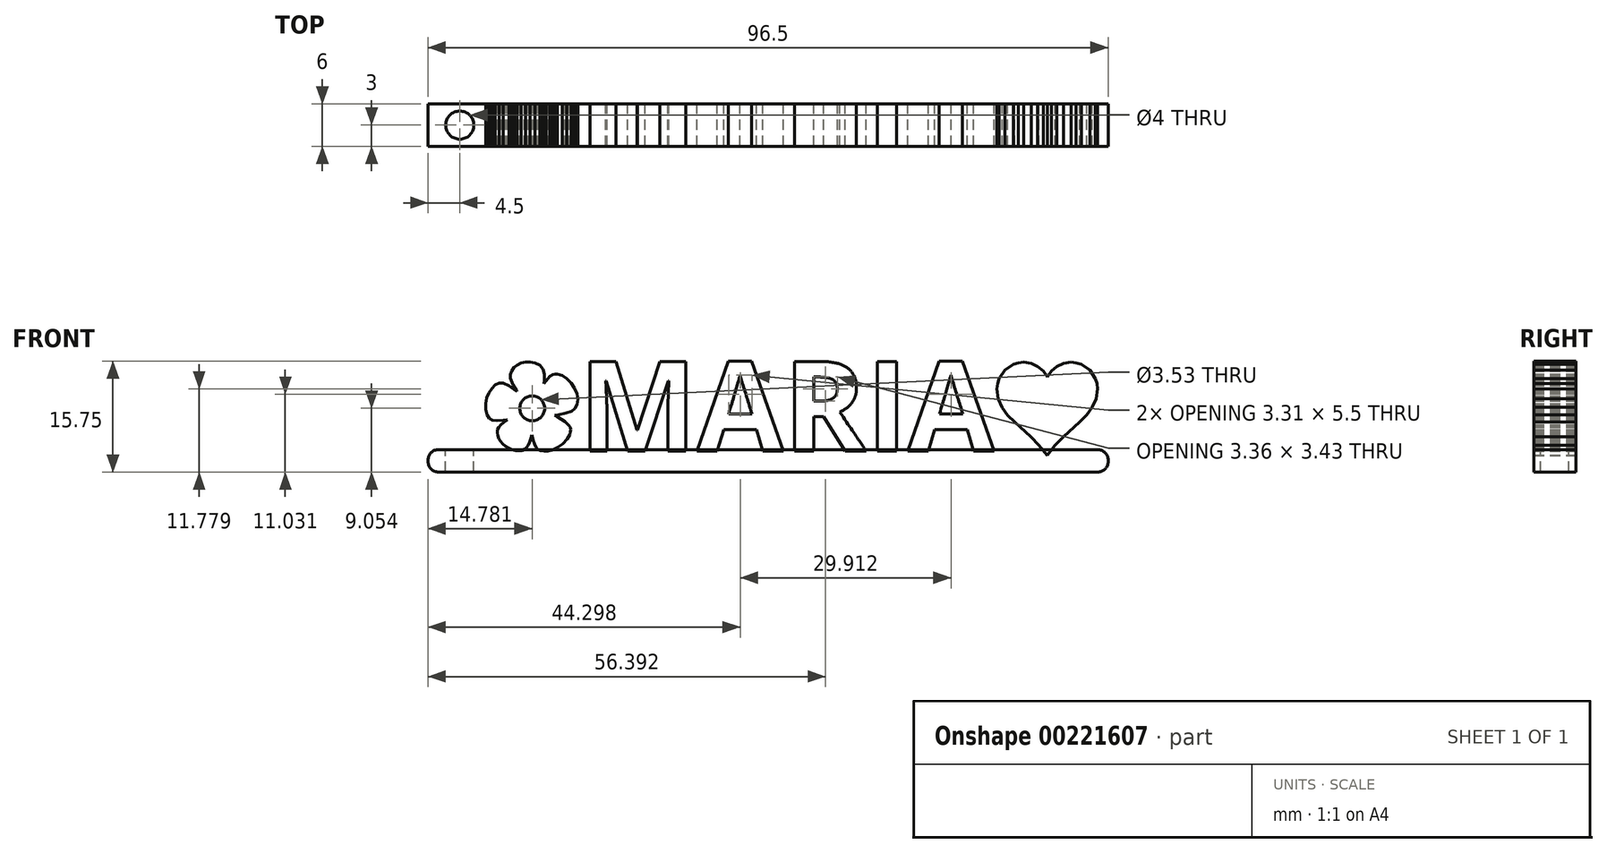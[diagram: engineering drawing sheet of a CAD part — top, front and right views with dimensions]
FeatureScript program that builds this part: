
annotation { "Feature Type Name" : "Feature", "Feature Type Description" : "" }
export const myFeature = defineFeature(function(context is Context, id is Id, definition is map)
    precondition{}
    {
        {
            var Q0;
            Q0=qCreatedBy(makeId("Front.planeOp"),FACE);
            var sketch = newSketch(context, id + "F0", { "sketchPlane" : qUnion([Q0])});
            skText(sketch, "E0", { "text": "   MARIA", "fontName": "OpenSans-Bold.ttf"});
            skLineSegment(sketch, "E1.0.0", {"start": v(-9.3, 0.1) * mm, "end": v(-8.53, 0.46) * mm});
            skLineSegment(sketch, "E1.0.1", {"start": v(-8.53, 0.46) * mm, "end": v(-7.79, 1.02) * mm});
            skLineSegment(sketch, "E1.0.2", {"start": v(-7.79, 1.02) * mm, "end": v(-7.18, 1.67) * mm});
            skLineSegment(sketch, "E1.0.3", {"start": v(-7.18, 1.67) * mm, "end": v(-6.78, 2.35) * mm});
            skLineSegment(sketch, "E1.0.4", {"start": v(-6.78, 2.35) * mm, "end": v(-6.68, 2.7) * mm});
            skLineSegment(sketch, "E1.0.5", {"start": v(-6.68, 2.7) * mm, "end": v(-6.67, 3.02) * mm});
            skLineSegment(sketch, "E1.0.6", {"start": v(-6.67, 3.02) * mm, "end": v(-6.73, 3.33) * mm});
            skLineSegment(sketch, "E1.0.7", {"start": v(-6.73, 3.33) * mm, "end": v(-6.89, 3.62) * mm});
            skLineSegment(sketch, "E1.0.8", {"start": v(-6.89, 3.62) * mm, "end": v(-7.48, 4.2) * mm});
            skLineSegment(sketch, "E1.0.9", {"start": v(-7.48, 4.2) * mm, "end": v(-8.5, 4.79) * mm});
            skLineSegment(sketch, "E1.0.10", {"start": v(-8.5, 4.79) * mm, "end": v(-8.93, 5.06) * mm});
            skLineSegment(sketch, "E1.0.11", {"start": v(-8.93, 5.06) * mm, "end": v(-8.42, 5.16) * mm});
            skLineSegment(sketch, "E1.0.12", {"start": v(-8.42, 5.16) * mm, "end": v(-7.31, 5.37) * mm});
            skLineSegment(sketch, "E1.0.13", {"start": v(-7.31, 5.37) * mm, "end": v(-6.55, 5.65) * mm});
            skLineSegment(sketch, "E1.0.14", {"start": v(-6.55, 5.65) * mm, "end": v(-6.05, 6.04) * mm});
            skLineSegment(sketch, "E1.0.15", {"start": v(-6.05, 6.04) * mm, "end": v(-5.76, 6.58) * mm});
            skLineSegment(sketch, "E1.0.16", {"start": v(-5.76, 6.58) * mm, "end": v(-5.64, 7.33) * mm});
            skLineSegment(sketch, "E1.0.17", {"start": v(-5.64, 7.33) * mm, "end": v(-5.78, 8.14) * mm});
            skLineSegment(sketch, "E1.0.18", {"start": v(-5.78, 8.14) * mm, "end": v(-6.1, 8.93) * mm});
            skLineSegment(sketch, "E1.0.19", {"start": v(-6.1, 8.93) * mm, "end": v(-6.6, 9.67) * mm});
            skLineSegment(sketch, "E1.0.20", {"start": v(-6.6, 9.67) * mm, "end": v(-7.2, 10.28) * mm});
            skLineSegment(sketch, "E1.0.21", {"start": v(-7.2, 10.28) * mm, "end": v(-7.86, 10.72) * mm});
            skLineSegment(sketch, "E1.0.22", {"start": v(-7.86, 10.72) * mm, "end": v(-8.55, 10.93) * mm});
            skLineSegment(sketch, "E1.0.23", {"start": v(-8.55, 10.93) * mm, "end": v(-8.88, 10.93) * mm});
            skLineSegment(sketch, "E1.0.24", {"start": v(-8.88, 10.93) * mm, "end": v(-9.2, 10.85) * mm});
            skLineSegment(sketch, "E1.0.25", {"start": v(-9.2, 10.85) * mm, "end": v(-9.65, 10.56) * mm});
            skLineSegment(sketch, "E1.0.26", {"start": v(-9.65, 10.56) * mm, "end": v(-10.14, 9.98) * mm});
            skLineSegment(sketch, "E1.0.27", {"start": v(-10.14, 9.98) * mm, "end": v(-10.45, 9.58) * mm});
            skLineSegment(sketch, "E1.0.28", {"start": v(-10.45, 9.58) * mm, "end": v(-10.4, 10.03) * mm});
            skLineSegment(sketch, "E1.0.29", {"start": v(-10.4, 10.03) * mm, "end": v(-10.4, 10.93) * mm});
            skLineSegment(sketch, "E1.0.30", {"start": v(-10.4, 10.93) * mm, "end": v(-10.6, 11.63) * mm});
            skLineSegment(sketch, "E1.0.31", {"start": v(-10.6, 11.63) * mm, "end": v(-11.04, 12.15) * mm});
            skLineSegment(sketch, "E1.0.32", {"start": v(-11.04, 12.15) * mm, "end": v(-11.71, 12.5) * mm});
            skLineSegment(sketch, "E1.0.33", {"start": v(-11.71, 12.5) * mm, "end": v(-12.4, 12.64) * mm});
            skLineSegment(sketch, "E1.0.34", {"start": v(-12.4, 12.64) * mm, "end": v(-13.07, 12.62) * mm});
            skLineSegment(sketch, "E1.0.35", {"start": v(-13.07, 12.62) * mm, "end": v(-13.7, 12.47) * mm});
            skLineSegment(sketch, "E1.0.36", {"start": v(-13.7, 12.47) * mm, "end": v(-14.26, 12.2) * mm});
            skLineSegment(sketch, "E1.0.37", {"start": v(-14.26, 12.2) * mm, "end": v(-14.72, 11.83) * mm});
            skLineSegment(sketch, "E1.0.38", {"start": v(-14.72, 11.83) * mm, "end": v(-15.05, 11.38) * mm});
            skLineSegment(sketch, "E1.0.39", {"start": v(-15.05, 11.38) * mm, "end": v(-15.22, 10.87) * mm});
            skLineSegment(sketch, "E1.0.40", {"start": v(-15.22, 10.87) * mm, "end": v(-15.2, 10.3) * mm});
            skLineSegment(sketch, "E1.0.41", {"start": v(-15.2, 10.3) * mm, "end": v(-14.83, 9.4) * mm});
            skLineSegment(sketch, "E1.0.42", {"start": v(-14.83, 9.4) * mm, "end": v(-14.35, 8.55) * mm});
            skLineSegment(sketch, "E1.0.43", {"start": v(-14.35, 8.55) * mm, "end": v(-14.3, 8.4) * mm});
            skLineSegment(sketch, "E1.0.44", {"start": v(-14.3, 8.4) * mm, "end": v(-14.48, 8.53) * mm});
            skLineSegment(sketch, "E1.0.45", {"start": v(-14.48, 8.53) * mm, "end": v(-15.4, 9.23) * mm});
            skLineSegment(sketch, "E1.0.46", {"start": v(-15.4, 9.23) * mm, "end": v(-16.22, 9.63) * mm});
            skLineSegment(sketch, "E1.0.47", {"start": v(-16.22, 9.63) * mm, "end": v(-16.8, 9.63) * mm});
            skLineSegment(sketch, "E1.0.48", {"start": v(-16.8, 9.63) * mm, "end": v(-17.36, 9.37) * mm});
            skLineSegment(sketch, "E1.0.49", {"start": v(-17.36, 9.37) * mm, "end": v(-17.85, 8.9) * mm});
            skLineSegment(sketch, "E1.0.50", {"start": v(-17.85, 8.9) * mm, "end": v(-18.26, 8.26) * mm});
            skLineSegment(sketch, "E1.0.51", {"start": v(-18.26, 8.26) * mm, "end": v(-18.56, 7.51) * mm});
            skLineSegment(sketch, "E1.0.52", {"start": v(-18.56, 7.51) * mm, "end": v(-18.72, 6.71) * mm});
            skLineSegment(sketch, "E1.0.53", {"start": v(-18.72, 6.71) * mm, "end": v(-18.72, 5.9) * mm});
            skLineSegment(sketch, "E1.0.54", {"start": v(-18.72, 5.9) * mm, "end": v(-18.52, 5.16) * mm});
            skLineSegment(sketch, "E1.0.55", {"start": v(-18.52, 5.16) * mm, "end": v(-18.2, 4.64) * mm});
            skLineSegment(sketch, "E1.0.56", {"start": v(-18.2, 4.64) * mm, "end": v(-17.75, 4.36) * mm});
            skLineSegment(sketch, "E1.0.57", {"start": v(-17.75, 4.36) * mm, "end": v(-17.1, 4.27) * mm});
            skLineSegment(sketch, "E1.0.58", {"start": v(-17.1, 4.27) * mm, "end": v(-16.21, 4.37) * mm});
            skLineSegment(sketch, "E1.0.59", {"start": v(-16.21, 4.37) * mm, "end": v(-15.7, 4.43) * mm});
            skLineSegment(sketch, "E1.0.60", {"start": v(-15.7, 4.43) * mm, "end": v(-15.67, 4.4) * mm});
            skLineSegment(sketch, "E1.0.61", {"start": v(-15.67, 4.4) * mm, "end": v(-15.78, 4.33) * mm});
            skLineSegment(sketch, "E1.0.62", {"start": v(-15.78, 4.33) * mm, "end": v(-16.17, 4.07) * mm});
            skLineSegment(sketch, "E1.0.63", {"start": v(-16.17, 4.07) * mm, "end": v(-16.55, 3.71) * mm});
            skLineSegment(sketch, "E1.0.64", {"start": v(-16.55, 3.71) * mm, "end": v(-16.87, 3.33) * mm});
            skLineSegment(sketch, "E1.0.65", {"start": v(-16.87, 3.33) * mm, "end": v(-17.04, 3) * mm});
            skLineSegment(sketch, "E1.0.66", {"start": v(-17.04, 3) * mm, "end": v(-17.08, 2.6) * mm});
            skLineSegment(sketch, "E1.0.67", {"start": v(-17.08, 2.6) * mm, "end": v(-17.02, 2.2) * mm});
            skLineSegment(sketch, "E1.0.68", {"start": v(-17.02, 2.2) * mm, "end": v(-16.87, 1.78) * mm});
            skLineSegment(sketch, "E1.0.69", {"start": v(-16.87, 1.78) * mm, "end": v(-16.62, 1.39) * mm});
            skLineSegment(sketch, "E1.0.70", {"start": v(-16.62, 1.39) * mm, "end": v(-16.3, 1.02) * mm});
            skLineSegment(sketch, "E1.0.71", {"start": v(-16.3, 1.02) * mm, "end": v(-15.9, 0.69) * mm});
            skLineSegment(sketch, "E1.0.72", {"start": v(-15.9, 0.69) * mm, "end": v(-15.45, 0.4) * mm});
            skLineSegment(sketch, "E1.0.73", {"start": v(-15.45, 0.4) * mm, "end": v(-14.95, 0.2) * mm});
            skLineSegment(sketch, "E1.0.74", {"start": v(-14.95, 0.2) * mm, "end": v(-14.44, 0.06) * mm});
            skLineSegment(sketch, "E1.0.75", {"start": v(-14.44, 0.06) * mm, "end": v(-13.98, 0.02) * mm});
            skLineSegment(sketch, "E1.0.76", {"start": v(-13.98, 0.02) * mm, "end": v(-13.58, 0.08) * mm});
            skLineSegment(sketch, "E1.0.77", {"start": v(-13.58, 0.08) * mm, "end": v(-13.23, 0.23) * mm});
            skLineSegment(sketch, "E1.0.78", {"start": v(-13.23, 0.23) * mm, "end": v(-12.92, 0.49) * mm});
            skLineSegment(sketch, "E1.0.79", {"start": v(-12.92, 0.49) * mm, "end": v(-12.67, 0.84) * mm});
            skLineSegment(sketch, "E1.0.80", {"start": v(-12.67, 0.84) * mm, "end": v(-12.46, 1.28) * mm});
            skLineSegment(sketch, "E1.0.81", {"start": v(-12.46, 1.28) * mm, "end": v(-12.3, 1.83) * mm});
            skLineSegment(sketch, "E1.0.82", {"start": v(-12.3, 1.83) * mm, "end": v(-12.19, 2.26) * mm});
            skLineSegment(sketch, "E1.0.83", {"start": v(-12.19, 2.26) * mm, "end": v(-12.13, 2.1) * mm});
            skLineSegment(sketch, "E1.0.84", {"start": v(-12.13, 2.1) * mm, "end": v(-12.01, 1.53) * mm});
            skLineSegment(sketch, "E1.0.85", {"start": v(-12.01, 1.53) * mm, "end": v(-11.82, 1) * mm});
            skLineSegment(sketch, "E1.0.86", {"start": v(-11.82, 1) * mm, "end": v(-11.6, 0.55) * mm});
            skLineSegment(sketch, "E1.0.87", {"start": v(-11.6, 0.55) * mm, "end": v(-11.35, 0.26) * mm});
            skLineSegment(sketch, "E1.0.88", {"start": v(-11.35, 0.26) * mm, "end": v(-10.95, 0.05) * mm});
            skLineSegment(sketch, "E1.0.89", {"start": v(-10.95, 0.05) * mm, "end": v(-10.46, -0.04) * mm});
            skLineSegment(sketch, "E1.0.90", {"start": v(-10.46, -0.04) * mm, "end": v(-9.9, -0.03) * mm});
            skLineSegment(sketch, "E1.0.91", {"start": v(-9.9, -0.03) * mm, "end": v(-9.3, 0.1) * mm});
            skCircle(sketch, "E2", {"center": v(-12.12, 6.05) * mm, "radius": 1.77 * mm});
            skLineSegment(sketch, "E3", {"start": v(57.6, 12.6) * mm, "end": v(56.84, 12.52) * mm});
            skLineSegment(sketch, "E4", {"start": v(56.84, 12.52) * mm, "end": v(56.13, 12.3) * mm});
            skLineSegment(sketch, "E5", {"start": v(56.13, 12.3) * mm, "end": v(54.94, 11.5) * mm});
            skLineSegment(sketch, "E6", {"start": v(54.94, 11.5) * mm, "end": v(54.13, 10.3) * mm});
            skLineSegment(sketch, "E7", {"start": v(54.13, 10.3) * mm, "end": v(53.9, 9.59) * mm});
            skLineSegment(sketch, "E8", {"start": v(53.9, 9.59) * mm, "end": v(53.83, 8.83) * mm});
            skLineSegment(sketch, "E9", {"start": v(53.83, 8.83) * mm, "end": v(54.02, 7.39) * mm});
            skLineSegment(sketch, "E10", {"start": v(54.02, 7.39) * mm, "end": v(54.54, 6.16) * mm});
            skLineSegment(sketch, "E11", {"start": v(54.54, 6.16) * mm, "end": v(55.33, 5.08) * mm});
            skLineSegment(sketch, "E12", {"start": v(55.33, 5.08) * mm, "end": v(56.31, 4.08) * mm});
            skLineSegment(sketch, "E13", {"start": v(56.31, 4.08) * mm, "end": v(58.6, 2.03) * mm});
            skLineSegment(sketch, "E14", {"start": v(58.6, 2.03) * mm, "end": v(59.8, 0.82) * mm});
            skLineSegment(sketch, "E15", {"start": v(59.8, 0.82) * mm, "end": v(60.92, -0.59) * mm});
            skLineSegment(sketch, "E16", {"start": v(60.92, -0.59) * mm, "end": v(60.96, -0.65) * mm});
            skLineSegment(sketch, "E17", {"start": v(60.96, -0.65) * mm, "end": v(61, -0.59) * mm});
            skLineSegment(sketch, "E18", {"start": v(61, -0.59) * mm, "end": v(62.08, 0.82) * mm});
            skLineSegment(sketch, "E19", {"start": v(62.08, 0.82) * mm, "end": v(63.24, 2.03) * mm});
            skLineSegment(sketch, "E20", {"start": v(63.24, 2.03) * mm, "end": v(65.55, 4.12) * mm});
            skLineSegment(sketch, "E21", {"start": v(65.55, 4.12) * mm, "end": v(66.55, 5.13) * mm});
            skLineSegment(sketch, "E22", {"start": v(66.55, 5.13) * mm, "end": v(67.35, 6.21) * mm});
            skLineSegment(sketch, "E23", {"start": v(67.35, 6.21) * mm, "end": v(67.89, 7.42) * mm});
            skLineSegment(sketch, "E24", {"start": v(67.89, 7.42) * mm, "end": v(68.08, 8.83) * mm});
            skLineSegment(sketch, "E25", {"start": v(68.08, 8.83) * mm, "end": v(68, 9.59) * mm});
            skLineSegment(sketch, "E26", {"start": v(68, 9.59) * mm, "end": v(67.79, 10.3) * mm});
            skLineSegment(sketch, "E27", {"start": v(67.79, 10.3) * mm, "end": v(66.98, 11.5) * mm});
            skLineSegment(sketch, "E28", {"start": v(66.98, 11.5) * mm, "end": v(65.78, 12.3) * mm});
            skLineSegment(sketch, "E29", {"start": v(65.78, 12.3) * mm, "end": v(65.08, 12.52) * mm});
            skLineSegment(sketch, "E30", {"start": v(65.08, 12.52) * mm, "end": v(64.32, 12.6) * mm});
            skLineSegment(sketch, "E31", {"start": v(64.32, 12.6) * mm, "end": v(63.26, 12.44) * mm});
            skLineSegment(sketch, "E32", {"start": v(63.26, 12.44) * mm, "end": v(62.32, 12.01) * mm});
            skLineSegment(sketch, "E33", {"start": v(62.32, 12.01) * mm, "end": v(61.54, 11.35) * mm});
            skLineSegment(sketch, "E34", {"start": v(61.54, 11.35) * mm, "end": v(60.96, 10.5) * mm});
            skLineSegment(sketch, "E35", {"start": v(60.96, 10.5) * mm, "end": v(60.38, 11.35) * mm});
            skLineSegment(sketch, "E36", {"start": v(60.38, 11.35) * mm, "end": v(59.6, 12.01) * mm});
            skLineSegment(sketch, "E37", {"start": v(59.6, 12.01) * mm, "end": v(58.66, 12.44) * mm});
            skLineSegment(sketch, "E38", {"start": v(58.66, 12.44) * mm, "end": v(57.6, 12.6) * mm});
            skLineSegment(sketch, "E39", {"start": v(54.6, 12.81) * mm, "end": v(73.38, 12.81) * mm, "construction": true});
            const initialGuessF0  = {"E0": [-0.0194, 0, 1, 0, 0.01281]};
            skSetInitialGuess(sketch, initialGuessF0);
            skSolve(sketch);
        }
        {
            var Q0;
            Q0=qSketchRegion(id+"F0",true);
            extrude(context, id + "F1", {"entities" : qUnion([Q0]), "endBound" : BoundingType.SYMMETRIC, "depth" : 6 * mm});
        }
        {
            var Q0;
            Q0=qCreatedBy(makeId("Top.planeOp"),FACE);
            var sketch = newSketch(context, id + "F2", { "sketchPlane" : qUnion([Q0])});
            skLineSegment(sketch, "E40.bottom", {"start": v(-19.4, 3) * mm, "end": v(69.6, 3) * mm});
            skLineSegment(sketch, "E40.top", {"start": v(-19.4, -3) * mm, "end": v(69.6, -3) * mm});
            skLineSegment(sketch, "E40.left", {"start": v(-19.4, 3) * mm, "end": v(-19.4, -3) * mm});
            skLineSegment(sketch, "E40.right", {"start": v(69.6, 3) * mm, "end": v(69.6, -3) * mm});
            skSolve(sketch);
        }
        {
            var Q0;
            Q0=makeQuery(id+"F2.imprint","IMPRINT",FACE,{"disambiguationData":[TD([[makeQuery(id+"F2.imprint","IMPRINT",EDGE,{"derivedFrom":sQuery(id+"F2.wireOp",EDGE,"E40.bottom")}),-1.0]])]});
            extrude(context, id + "F3", {"entities" : qUnion([Q0]), "depth" : 0.2 * mm});
        }
        {
            var Q0;
            Q0=makeQuery(id+"F3.opExtrude","CAP_FACE",FACE,{"disambiguationData":[OSD([sQuery(id+"F2.wireOp",EDGE,"E40.bottom"),sQuery(id+"F2.wireOp",EDGE,"E40.top"),sQuery(id+"F2.wireOp",EDGE,"E40.left"),sQuery(id+"F2.wireOp",EDGE,"E40.right")])],"isStart":true});
            extrude(context, id + "F4", {"entities" : qUnion([Q0]), "depth" : 3 * mm});
        }
        {
            var Q0;
            {var subQ0=sQuery(id+"F2.wireOp",EDGE,"E40.left");Q0=makeQuery(id+"FaVoHrOpcFZXiYX_6.opBoolean","MERGE",FACE,{"derivedFrom":[makeQuery(id+"F3.opExtrude","SWEPT_FACE",FACE,{"disambiguationData":[OSD([subQ0])]}),makeQuery(id+"F4.opExtrude","SWEPT_FACE",FACE,{"disambiguationData":[OSD([subQ0])]})]});}
            var sketch = newSketch(context, id + "F5", { "sketchPlane" : qUnion([Q0])});
            skLineSegment(sketch, "E41.bottom", {"start": v(-3, -3) * mm, "end": v(3, -3) * mm});
            skLineSegment(sketch, "E41.top", {"start": v(-3, 0.2) * mm, "end": v(3, 0.2) * mm});
            skLineSegment(sketch, "E41.left", {"start": v(-3, -3) * mm, "end": v(-3, 0.2) * mm});
            skLineSegment(sketch, "E41.right", {"start": v(3, -3) * mm, "end": v(3, 0.2) * mm});
            skSolve(sketch);
        }
        {
            var Q0;
            Q0=qSketchRegion(id+"F5",true);
            extrude(context, id + "F6", {"entities" : qUnion([Q0]), "operationType" : NewBodyOperationType.ADD, "depth" : 7.5 * mm});
        }
        {
            var Q0;
            Q0=makeQuery(id+"F6.opExtrude","CAP_EDGE",EDGE,{"disambiguationData":[OSD([sQuery(id+"F5.wireOp",EDGE,"E41.bottom")])],"isStart":false});
            var Q1;
            Q1=makeQuery(id+"F6.opExtrude","CAP_EDGE",EDGE,{"disambiguationData":[OSD([sQuery(id+"F5.wireOp",EDGE,"E41.top")])],"isStart":false});
            var Q2;
            Q2=makeQuery(id+"F4.opExtrude","CAP_EDGE",EDGE,{"disambiguationData":[OSD([sQuery(id+"F2.wireOp",EDGE,"E40.right")])],"isStart":false});
            fillet(context, id + "F7", {"entities" : qUnion([Q0, Q1, Q2]), "radius" : 1.5 * mm, "tangentPropagation" : true, "allowEdgeOverflow" : false});
        }
        {
            var Q0;
            {var subQ19=sQuery(id+"F2.wireOp",EDGE,"E40.top");var subQ20=sQuery(id+"F2.wireOp",EDGE,"E40.bottom");var subQ63=sQuery(id+"F0.wireOp",EDGE,"E0.sketch_text.stroke-2");var subQ66=sQuery(id+"F2.wireOp",EDGE,"E40.left");Q0=makeQuery(id+"F6.boolean.opBoolean","MERGE",FACE,{"derivedFrom":[makeQuery(id+"FaVoHrOpcFZXiYX_6.opBoolean","SPLIT",FACE,{"disambiguationData":[TD([makeQuery(id+"F1.opExtrude","SWEPT_FACE",FACE,{"disambiguationData":[OSD([subQ63])]})])],"derivedFrom":makeQuery(id+"F3.opExtrude","CAP_FACE",FACE,{"disambiguationData":[OSD([subQ20,subQ19,subQ66,sQuery(id+"F2.wireOp",EDGE,"E40.right")])],"isStart":false})}),makeQuery(id+"F6.opExtrude","SWEPT_FACE",FACE,{"disambiguationData":[OSD([sQuery(id+"F5.wireOp",EDGE,"E41.top")])]})]});}
            var sketch = newSketch(context, id + "F8", { "sketchPlane" : qUnion([Q0])});
            skCircle(sketch, "E42", {"center": v(-22.4, 0) * mm, "radius": 2 * mm});
            skSolve(sketch);
        }
        {
            var Q0;
            Q0=makeQuery(id+"F8.imprint","IMPRINT",FACE,{"disambiguationData":[TD([[makeQuery(id+"F8.imprint","IMPRINT",EDGE,{"derivedFrom":sQuery(id+"F8.wireOp",EDGE,"E42")}),1.0]])]});
            extrude(context, id + "F9", {"entities" : qUnion([Q0]), "operationType" : NewBodyOperationType.REMOVE, "oppositeDirection" : true, "depth" : 4 * mm});
        }
        {
            var Q0;
            Q0=makeQuery(id+"F3.opExtrude","CAP_EDGE",EDGE,{"disambiguationData":[OSD([sQuery(id+"F2.wireOp",EDGE,"E40.right")])],"isStart":false});
            fillet(context, id + "F10", {"entities" : qUnion([Q0]), "radius" : 1.5 * mm, "tangentPropagation" : true, "allowEdgeOverflow" : false});
        }
    });
